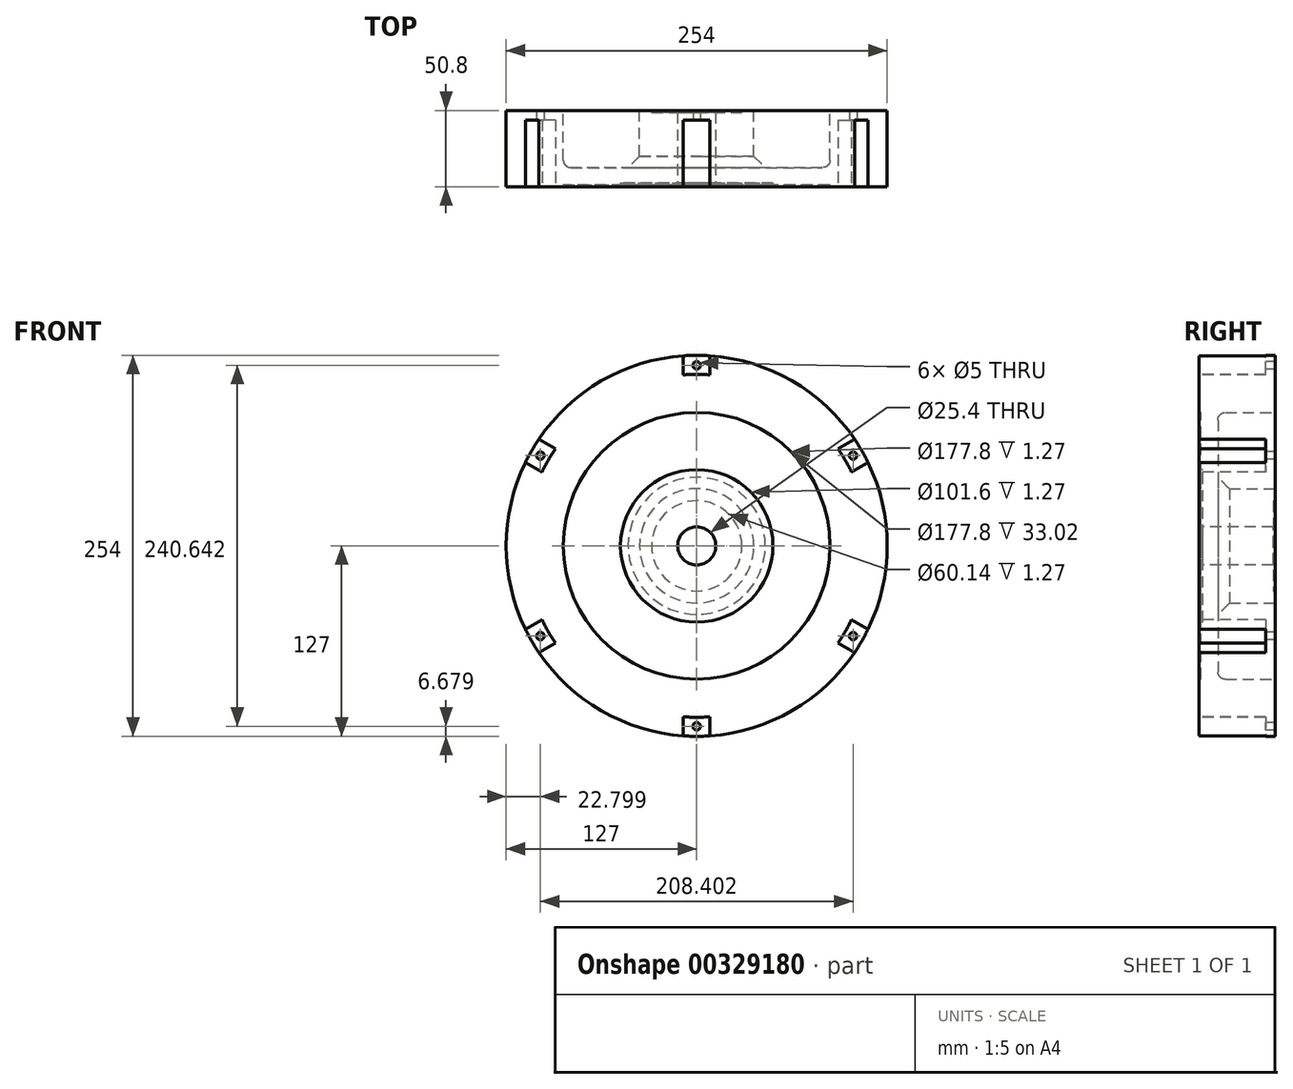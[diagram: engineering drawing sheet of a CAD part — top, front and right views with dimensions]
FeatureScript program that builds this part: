
annotation { "Feature Type Name" : "Feature", "Feature Type Description" : "" }
export const myFeature = defineFeature(function(context is Context, id is Id, definition is map)
    precondition{}
    {
        {
            var Q0;
            Q0=qCreatedBy(makeId("Front.planeOp"),FACE);
            var sketch = newSketch(context, id + "F0", { "sketchPlane" : qUnion([Q0])});
            skCircle(sketch, "E0", {"center": v(0, 0) * mm, "radius": 127 * mm});
            skSolve(sketch);
        }
        {
            var Q0;
            Q0=qSketchRegion(id+"F0",true);
            extrude(context, id + "F1", {"entities" : qUnion([Q0]), "depth" : 50.8 * mm});
        }
        {
            var Q0;
            Q0=makeQuery(id+"F1.opExtrude","CAP_FACE",FACE,{"disambiguationData":[OSD([sQuery(id+"F0.wireOp",EDGE,"E0")])],"isStart":false});
            var sketch = newSketch(context, id + "F2", { "sketchPlane" : qUnion([Q0])});
            skCircle(sketch, "E1", {"center": v(0, 0) * mm, "radius": 88.9 * mm});
            skSolve(sketch);
        }
        {
            var Q0;
            Q0=qSketchRegion(id+"F2",true);
            extrude(context, id + "F3", {"entities" : qUnion([Q0]), "operationType" : NewBodyOperationType.REMOVE, "oppositeDirection" : true, "depth" : 1.27 * mm});
        }
        {
            var Q0;
            Q0=makeQuery(id+"F3.boolean.opBoolean","COPY",FACE,{"derivedFrom":makeQuery(id+"F3.opExtrude","CAP_FACE",FACE,{"disambiguationData":[OSD([sQuery(id+"F2.wireOp",EDGE,"E1")])],"isStart":false})});
            var sketch = newSketch(context, id + "F4", { "sketchPlane" : qUnion([Q0])});
            skCircle(sketch, "E2", {"center": v(0, 0) * mm, "radius": 12.7 * mm});
            skPoint(sketch, "E3.center.orphan", {"position": v(35.62, 0) * mm});
            skSolve(sketch);
        }
        {
            var Q0;
            Q0=qSketchRegion(id+"F4",true);
            extrude(context, id + "F5", {"entities" : qUnion([Q0]), "operationType" : NewBodyOperationType.REMOVE, "oppositeDirection" : true, "depth" : 50.8 * mm});
        }
        {
            var Q0;
            Q0=makeQuery(id+"F3.boolean.opBoolean","COPY",FACE,{"derivedFrom":makeQuery(id+"F3.opExtrude","CAP_FACE",FACE,{"disambiguationData":[OSD([sQuery(id+"F2.wireOp",EDGE,"E1")])],"isStart":false})});
            var sketch = newSketch(context, id + "F6", { "sketchPlane" : qUnion([Q0])});
            skCircle(sketch, "E4", {"center": v(0, 0) * mm, "radius": 50.8 * mm});
            skSolve(sketch);
        }
        {
            var Q0;
            Q0=qSketchRegion(id+"F6",true);
            extrude(context, id + "F7", {"entities" : qUnion([Q0]), "operationType" : NewBodyOperationType.REMOVE, "oppositeDirection" : true, "depth" : 1.27 * mm});
        }
        {
            var Q0;
            Q0=makeQuery(id+"F1.opExtrude","CAP_FACE",FACE,{"disambiguationData":[OSD([sQuery(id+"F0.wireOp",EDGE,"E0")])],"isStart":true});
            var sketch = newSketch(context, id + "F8", { "sketchPlane" : qUnion([Q0])});
            skCircle(sketch, "E5.0", {"center": v(0, 0) * mm, "radius": 88.9 * mm});
            skCircle(sketch, "E6", {"center": v(0, 0) * mm, "radius": 38.1 * mm});
            skSolve(sketch);
        }
        {
            var Q0;
            Q0=qSketchRegion(id+"F8",true);
            extrude(context, id + "F9", {"entities" : qUnion([Q0]), "operationType" : NewBodyOperationType.REMOVE, "oppositeDirection" : true, "depth" : 38.1 * mm});
        }
        {
            var Q0;
            Q0=makeQuery(id+"F9.boolean.opBoolean","COPY",EDGE,{"derivedFrom":makeQuery(id+"F9.opExtrude","CAP_EDGE",EDGE,{"disambiguationData":[OSD([sQuery(id+"F8.wireOp",EDGE,"E6")])],"isStart":false})});
            chamfer(context, id + "F10", {"entities" : qUnion([Q0]), "width" : 7.62 * mm, "tangentPropagation" : true});
        }
        {
            var Q0;
            Q0=makeQuery(id+"F9.boolean.opBoolean","COPY",EDGE,{"derivedFrom":makeQuery(id+"F9.opExtrude","CAP_EDGE",EDGE,{"disambiguationData":[OSD([sQuery(id+"F8.wireOp",EDGE,"E5.0")])],"isStart":false})});
            fillet(context, id + "F11", {"entities" : qUnion([Q0]), "radius" : 5.08 * mm, "tangentPropagation" : true, "allowEdgeOverflow" : false});
        }
        {
            var Q0;
            Q0=makeQuery(id+"F1.opExtrude","CAP_FACE",FACE,{"disambiguationData":[OSD([sQuery(id+"F0.wireOp",EDGE,"E0")])],"isStart":false});
            var sketch = newSketch(context, id + "F12", { "sketchPlane" : qUnion([Q0])});
            skLineSegment(sketch, "E7", {"start": v(0, 127) * mm, "end": v(0, 107.95) * mm, "construction": true});
            skArc(sketch, "E8.0", {"start": v(3, 107.9) * mm, "mid": v(0, 107.95) * mm, "end": v(-3, 107.9) * mm});
            skLineSegment(sketch, "E9.0", {"start": v(-9.53, 127) * mm, "end": v(-9.53, 114.26) * mm});
            skLineSegment(sketch, "E10.0", {"start": v(9.53, 127) * mm, "end": v(9.53, 114.26) * mm});
            skPoint(sketch, "E11.visualSharp", {"position": v(-9.52, 107.53) * mm});
            skArc(sketch, "E11.filletArc", {"start": v(-9.53, 114.26) * mm, "mid": v(-7.6, 109.7) * mm, "end": v(-3, 107.9) * mm});
            skPoint(sketch, "E12.visualSharp", {"position": v(9.53, 107.53) * mm});
            skArc(sketch, "E12.filletArc", {"start": v(3, 107.9) * mm, "mid": v(7.6, 109.7) * mm, "end": v(9.53, 114.26) * mm});
            skLineSegment(sketch, "E13", {"start": v(-9.53, 117.47) * mm, "end": v(9.53, 117.47) * mm, "construction": true});
            skPoint(sketch, "E13.startSnap0", {"position": v(0, 117.47) * mm});
            skArc(sketch, "E14.0", {"start": v(9.52, 126.64) * mm, "mid": v(0, 127) * mm, "end": v(-9.52, 126.64) * mm});
            skArc(sketch, "E15.1.0", {"start": v(-82.81, 96.28) * mm, "mid": v(-89.8, 89.8) * mm, "end": v(-96.28, 82.81) * mm});
            skLineSegment(sketch, "E15.1.1", {"start": v(-83.07, 96.54) * mm, "end": v(-74.06, 87.53) * mm});
            skArc(sketch, "E15.1.2", {"start": v(-74.18, 78.42) * mm, "mid": v(-72.2, 82.95) * mm, "end": v(-74.06, 87.53) * mm});
            skArc(sketch, "E15.1.3", {"start": v(-74.18, 78.42) * mm, "mid": v(-76.33, 76.33) * mm, "end": v(-78.42, 74.18) * mm});
            skArc(sketch, "E15.1.4", {"start": v(-87.53, 74.06) * mm, "mid": v(-82.95, 72.2) * mm, "end": v(-78.42, 74.18) * mm});
            skLineSegment(sketch, "E15.1.5", {"start": v(-96.54, 83.07) * mm, "end": v(-87.53, 74.06) * mm});
            skArc(sketch, "E15.2.0", {"start": v(-126.64, 9.52) * mm, "mid": v(-127, 0) * mm, "end": v(-126.64, -9.52) * mm});
            skLineSegment(sketch, "E15.2.1", {"start": v(-127, 9.53) * mm, "end": v(-114.26, 9.53) * mm});
            skArc(sketch, "E15.2.2", {"start": v(-107.9, 3) * mm, "mid": v(-109.7, 7.6) * mm, "end": v(-114.26, 9.53) * mm});
            skArc(sketch, "E15.2.3", {"start": v(-107.9, 3) * mm, "mid": v(-107.95, 0) * mm, "end": v(-107.9, -3) * mm});
            skArc(sketch, "E15.2.4", {"start": v(-114.26, -9.52) * mm, "mid": v(-109.7, -7.6) * mm, "end": v(-107.9, -3) * mm});
            skLineSegment(sketch, "E15.2.5", {"start": v(-127, -9.52) * mm, "end": v(-114.26, -9.52) * mm});
            skArc(sketch, "E15.3.0", {"start": v(-96.28, -82.81) * mm, "mid": v(-89.8, -89.8) * mm, "end": v(-82.81, -96.28) * mm});
            skLineSegment(sketch, "E15.3.1", {"start": v(-96.54, -83.07) * mm, "end": v(-87.53, -74.06) * mm});
            skArc(sketch, "E15.3.2", {"start": v(-78.42, -74.18) * mm, "mid": v(-82.95, -72.2) * mm, "end": v(-87.53, -74.06) * mm});
            skArc(sketch, "E15.3.3", {"start": v(-78.42, -74.18) * mm, "mid": v(-76.33, -76.33) * mm, "end": v(-74.18, -78.42) * mm});
            skArc(sketch, "E15.3.4", {"start": v(-74.06, -87.53) * mm, "mid": v(-72.2, -82.95) * mm, "end": v(-74.18, -78.42) * mm});
            skLineSegment(sketch, "E15.3.5", {"start": v(-83.07, -96.54) * mm, "end": v(-74.06, -87.53) * mm});
            skArc(sketch, "E15.4.0", {"start": v(-9.53, -126.64) * mm, "mid": v(0, -127) * mm, "end": v(9.52, -126.64) * mm});
            skLineSegment(sketch, "E15.4.1", {"start": v(-9.53, -127) * mm, "end": v(-9.53, -114.26) * mm});
            skArc(sketch, "E15.4.2", {"start": v(-3, -107.9) * mm, "mid": v(-7.6, -109.7) * mm, "end": v(-9.53, -114.26) * mm});
            skArc(sketch, "E15.4.3", {"start": v(-3, -107.9) * mm, "mid": v(0, -107.95) * mm, "end": v(3, -107.9) * mm});
            skArc(sketch, "E15.4.4", {"start": v(9.52, -114.26) * mm, "mid": v(7.6, -109.7) * mm, "end": v(3, -107.9) * mm});
            skLineSegment(sketch, "E15.4.5", {"start": v(9.52, -127) * mm, "end": v(9.52, -114.26) * mm});
            skArc(sketch, "E15.5.0", {"start": v(82.81, -96.28) * mm, "mid": v(89.8, -89.8) * mm, "end": v(96.28, -82.81) * mm});
            skLineSegment(sketch, "E15.5.1", {"start": v(83.07, -96.54) * mm, "end": v(74.06, -87.53) * mm});
            skArc(sketch, "E15.5.2", {"start": v(74.18, -78.42) * mm, "mid": v(72.2, -82.95) * mm, "end": v(74.06, -87.53) * mm});
            skArc(sketch, "E15.5.3", {"start": v(74.18, -78.42) * mm, "mid": v(76.33, -76.33) * mm, "end": v(78.42, -74.18) * mm});
            skArc(sketch, "E15.5.4", {"start": v(87.53, -74.06) * mm, "mid": v(82.95, -72.2) * mm, "end": v(78.42, -74.18) * mm});
            skLineSegment(sketch, "E15.5.5", {"start": v(96.54, -83.07) * mm, "end": v(87.53, -74.06) * mm});
            skArc(sketch, "E15.6.0", {"start": v(126.64, -9.53) * mm, "mid": v(127, 0) * mm, "end": v(126.64, 9.52) * mm});
            skLineSegment(sketch, "E15.6.1", {"start": v(127, -9.53) * mm, "end": v(114.26, -9.53) * mm});
            skArc(sketch, "E15.6.2", {"start": v(107.9, -3) * mm, "mid": v(109.7, -7.6) * mm, "end": v(114.26, -9.53) * mm});
            skArc(sketch, "E15.6.3", {"start": v(107.9, -3) * mm, "mid": v(107.95, 0) * mm, "end": v(107.9, 3) * mm});
            skArc(sketch, "E15.6.4", {"start": v(114.26, 9.52) * mm, "mid": v(109.7, 7.6) * mm, "end": v(107.9, 3) * mm});
            skLineSegment(sketch, "E15.6.5", {"start": v(127, 9.52) * mm, "end": v(114.26, 9.52) * mm});
            skArc(sketch, "E15.7.0", {"start": v(96.28, 82.81) * mm, "mid": v(89.8, 89.8) * mm, "end": v(82.81, 96.28) * mm});
            skLineSegment(sketch, "E15.7.1", {"start": v(96.54, 83.07) * mm, "end": v(87.53, 74.06) * mm});
            skArc(sketch, "E15.7.2", {"start": v(78.42, 74.18) * mm, "mid": v(82.95, 72.2) * mm, "end": v(87.53, 74.06) * mm});
            skArc(sketch, "E15.7.3", {"start": v(78.42, 74.18) * mm, "mid": v(76.33, 76.33) * mm, "end": v(74.18, 78.42) * mm});
            skArc(sketch, "E15.7.4", {"start": v(74.06, 87.53) * mm, "mid": v(72.2, 82.95) * mm, "end": v(74.18, 78.42) * mm});
            skLineSegment(sketch, "E15.7.5", {"start": v(83.07, 96.54) * mm, "end": v(74.06, 87.53) * mm});
            skSolve(sketch);
        }
        {
            var Q0;
            Q0=qSketchRegion(id+"F12",true);
            extrude(context, id + "F13", {"entities" : qUnion([Q0]), "operationType" : NewBodyOperationType.ADD, "oppositeDirection" : true, "depth" : 44.45 * mm});
        }
        {
            var Q0;
            Q0=makeQuery(id+"F9.boolean.opBoolean","SPLIT",FACE,{"disambiguationData":[TD([makeQuery(id+"F5.boolean.opBoolean","COPY",FACE,{"derivedFrom":makeQuery(id+"F5.opExtrude","SWEPT_FACE",FACE,{"disambiguationData":[OSD([sQuery(id+"F4.wireOp",EDGE,"E2")])]})})])],"derivedFrom":makeQuery(id+"F1.opExtrude","CAP_FACE",FACE,{"disambiguationData":[OSD([sQuery(id+"F0.wireOp",EDGE,"E0")])],"isStart":true})});
            var sketch = newSketch(context, id + "F14", { "sketchPlane" : qUnion([Q0])});
            skCircle(sketch, "E16", {"center": v(0, 0) * mm, "radius": 30.07 * mm});
            skCircle(sketch, "E17.0", {"center": v(0, 0) * mm, "radius": 12.7 * mm});
            skSolve(sketch);
        }
        {
            var Q0;
            Q0=qSketchRegion(id+"F14",true);
            extrude(context, id + "F15", {"entities" : qUnion([Q0]), "operationType" : NewBodyOperationType.REMOVE, "oppositeDirection" : true, "depth" : 1.27 * mm});
        }
        {
            var Q0;
            Q0=makeQuery(id+"F1.opExtrude","CAP_FACE",FACE,{"disambiguationData":[OSD([sQuery(id+"F0.wireOp",EDGE,"E0")])],"isStart":false});
            var sketch = newSketch(context, id + "F16", { "sketchPlane" : qUnion([Q0])});
            skLineSegment(sketch, "E18", {"start": v(0, 0) * mm, "end": v(0, 127) * mm, "construction": true});
            skArc(sketch, "E19.0", {"start": v(8.89, 126.69) * mm, "mid": v(0, 127) * mm, "end": v(-8.9, 126.69) * mm});
            skArc(sketch, "E20.0", {"start": v(8.89, 113.95) * mm, "mid": v(0, 114.3) * mm, "end": v(-8.9, 113.95) * mm});
            skLineSegment(sketch, "E21.0", {"start": v(8.9, 113.95) * mm, "end": v(8.9, 127) * mm});
            skLineSegment(sketch, "E22.MirrorCS", {"start": v(-8.9, 113.95) * mm, "end": v(-8.9, 127) * mm});
            skPoint(sketch, "E23.orphan", {"position": v(-8.9, 0) * mm});
            skPoint(sketch, "E24.orphan", {"position": v(8.9, 0) * mm});
            skArc(sketch, "E25.1.0", {"start": v(-94.24, 64.68) * mm, "mid": v(-98.99, 57.15) * mm, "end": v(-103.13, 49.28) * mm});
            skLineSegment(sketch, "E25.1.1", {"start": v(-94.24, 64.68) * mm, "end": v(-105.54, 71.2) * mm});
            skArc(sketch, "E25.1.2", {"start": v(-105.27, 71.04) * mm, "mid": v(-109.99, 63.5) * mm, "end": v(-114.16, 55.65) * mm});
            skLineSegment(sketch, "E25.1.3", {"start": v(-103.13, 49.28) * mm, "end": v(-114.43, 55.8) * mm});
            skArc(sketch, "E25.2.0", {"start": v(-103.13, -49.28) * mm, "mid": v(-98.99, -57.15) * mm, "end": v(-94.24, -64.68) * mm});
            skLineSegment(sketch, "E25.2.1", {"start": v(-103.13, -49.28) * mm, "end": v(-114.43, -55.8) * mm});
            skArc(sketch, "E25.2.2", {"start": v(-114.16, -55.65) * mm, "mid": v(-109.99, -63.5) * mm, "end": v(-105.27, -71.04) * mm});
            skLineSegment(sketch, "E25.2.3", {"start": v(-94.24, -64.68) * mm, "end": v(-105.54, -71.2) * mm});
            skArc(sketch, "E25.3.0", {"start": v(-8.89, -113.95) * mm, "mid": v(0, -114.3) * mm, "end": v(8.89, -113.95) * mm});
            skLineSegment(sketch, "E25.3.1", {"start": v(-8.9, -113.95) * mm, "end": v(-8.9, -127) * mm});
            skArc(sketch, "E25.3.2", {"start": v(-8.9, -126.69) * mm, "mid": v(0, -127) * mm, "end": v(8.89, -126.69) * mm});
            skLineSegment(sketch, "E25.3.3", {"start": v(8.89, -113.95) * mm, "end": v(8.89, -127) * mm});
            skArc(sketch, "E25.4.0", {"start": v(94.24, -64.68) * mm, "mid": v(98.99, -57.15) * mm, "end": v(103.13, -49.28) * mm});
            skLineSegment(sketch, "E25.4.1", {"start": v(94.24, -64.68) * mm, "end": v(105.54, -71.2) * mm});
            skArc(sketch, "E25.4.2", {"start": v(105.27, -71.04) * mm, "mid": v(109.99, -63.5) * mm, "end": v(114.16, -55.65) * mm});
            skLineSegment(sketch, "E25.4.3", {"start": v(103.13, -49.28) * mm, "end": v(114.43, -55.8) * mm});
            skArc(sketch, "E25.5.0", {"start": v(103.13, 49.28) * mm, "mid": v(98.99, 57.15) * mm, "end": v(94.24, 64.68) * mm});
            skLineSegment(sketch, "E25.5.1", {"start": v(103.13, 49.28) * mm, "end": v(114.43, 55.8) * mm});
            skArc(sketch, "E25.5.2", {"start": v(114.16, 55.65) * mm, "mid": v(109.99, 63.5) * mm, "end": v(105.27, 71.04) * mm});
            skLineSegment(sketch, "E25.5.3", {"start": v(94.24, 64.68) * mm, "end": v(105.54, 71.2) * mm});
            skSolve(sketch);
        }
        {
            var Q0;
            {var subQ0=sQuery(id+"F16.wireOp",EDGE,"E25.1.0");Q0=makeQuery(id+"F16.imprint","IMPRINT",FACE,{"disambiguationData":[TD([[makeQuery(id+"F16.imprint","IMPRINT",EDGE,{"derivedFrom":subQ0}),-1.0]])]});}
            var Q1;
            {var subQ0=sQuery(id+"F16.wireOp",EDGE,"E25.2.0");Q1=makeQuery(id+"F16.imprint","IMPRINT",FACE,{"disambiguationData":[TD([[makeQuery(id+"F16.imprint","IMPRINT",EDGE,{"derivedFrom":subQ0}),-1.0]])]});}
            var Q2;
            {var subQ0=sQuery(id+"F16.wireOp",EDGE,"E25.3.0");Q2=makeQuery(id+"F16.imprint","IMPRINT",FACE,{"disambiguationData":[TD([[makeQuery(id+"F16.imprint","IMPRINT",EDGE,{"derivedFrom":subQ0}),-1.0]])]});}
            var Q3;
            {var subQ0=sQuery(id+"F16.wireOp",EDGE,"E25.4.0");Q3=makeQuery(id+"F16.imprint","IMPRINT",FACE,{"disambiguationData":[TD([[makeQuery(id+"F16.imprint","IMPRINT",EDGE,{"derivedFrom":subQ0}),-1.0]])]});}
            var Q4;
            {var subQ0=sQuery(id+"F16.wireOp",EDGE,"E25.5.0");Q4=makeQuery(id+"F16.imprint","IMPRINT",FACE,{"disambiguationData":[TD([[makeQuery(id+"F16.imprint","IMPRINT",EDGE,{"derivedFrom":subQ0}),-1.0]])]});}
            var Q5;
            {var subQ0=sQuery(id+"F16.wireOp",EDGE,"E19.0");Q5=makeQuery(id+"F16.imprint","IMPRINT",FACE,{"disambiguationData":[TD([[makeQuery(id+"F16.imprint","IMPRINT",EDGE,{"derivedFrom":subQ0}),1.0]])]});}
            extrude(context, id + "F17", {"entities" : qUnion([Q0, Q1, Q2, Q3, Q4, Q5]), "operationType" : NewBodyOperationType.REMOVE, "oppositeDirection" : true, "depth" : 44.45 * mm});
        }
        {
            var Q0;
            Q0=makeQuery(id+"F17.boolean.opBoolean","COPY",FACE,{"derivedFrom":makeQuery(id+"F17.opExtrude","CAP_FACE",FACE,{"disambiguationData":[OSD([sQuery(id+"F16.wireOp",EDGE,"E19.0"),sQuery(id+"F16.wireOp",EDGE,"E20.0"),sQuery(id+"F16.wireOp",EDGE,"E21.0"),sQuery(id+"F16.wireOp",EDGE,"E22.MirrorCS")])],"isStart":false})});
            var sketch = newSketch(context, id + "F18", { "sketchPlane" : qUnion([Q0])});
            skLineSegment(sketch, "E26", {"start": v(0, 114.3) * mm, "end": v(0, 127) * mm, "construction": true});
            skLineSegment(sketch, "E27.1.0", {"start": v(-98.99, 57.15) * mm, "end": v(-109.99, 63.5) * mm, "construction": true});
            skLineSegment(sketch, "E27.2.0", {"start": v(-98.99, -57.15) * mm, "end": v(-109.99, -63.5) * mm, "construction": true});
            skLineSegment(sketch, "E27.3.0", {"start": v(0, -114.3) * mm, "end": v(0, -127) * mm, "construction": true});
            skLineSegment(sketch, "E27.4.0", {"start": v(98.99, -57.15) * mm, "end": v(109.99, -63.5) * mm, "construction": true});
            skLineSegment(sketch, "E27.5.0", {"start": v(98.99, 57.15) * mm, "end": v(109.99, 63.5) * mm, "construction": true});
            skPoint(sketch, "E27.center", {"position": v(0, 0) * mm});
            skCircle(sketch, "E28", {"center": v(0, 120.32) * mm, "radius": 2.5 * mm});
            skPoint(sketch, "E28.centerSnap0", {"position": v(-8.9, 120.32) * mm});
            skCircle(sketch, "E29.1.0", {"center": v(-104.2, 60.16) * mm, "radius": 2.5 * mm});
            skCircle(sketch, "E29.2.0", {"center": v(-104.2, -60.16) * mm, "radius": 2.5 * mm});
            skCircle(sketch, "E30.1.3.0", {"center": v(0, -120.32) * mm, "radius": 2.5 * mm});
            skCircle(sketch, "E30.1.4.0", {"center": v(104.2, -60.16) * mm, "radius": 2.5 * mm});
            skCircle(sketch, "E30.1.5.0", {"center": v(104.2, 60.16) * mm, "radius": 2.5 * mm});
            skSolve(sketch);
        }
        {
            var Q0;
            Q0 = qSketchRegion(id + "F18", true);
            extrude(context, id + "F19", {"entities" : qUnion([Q0]), "operationType" : NewBodyOperationType.REMOVE, "oppositeDirection" : true, "depth" : 25.4 * mm});
        }
    });
